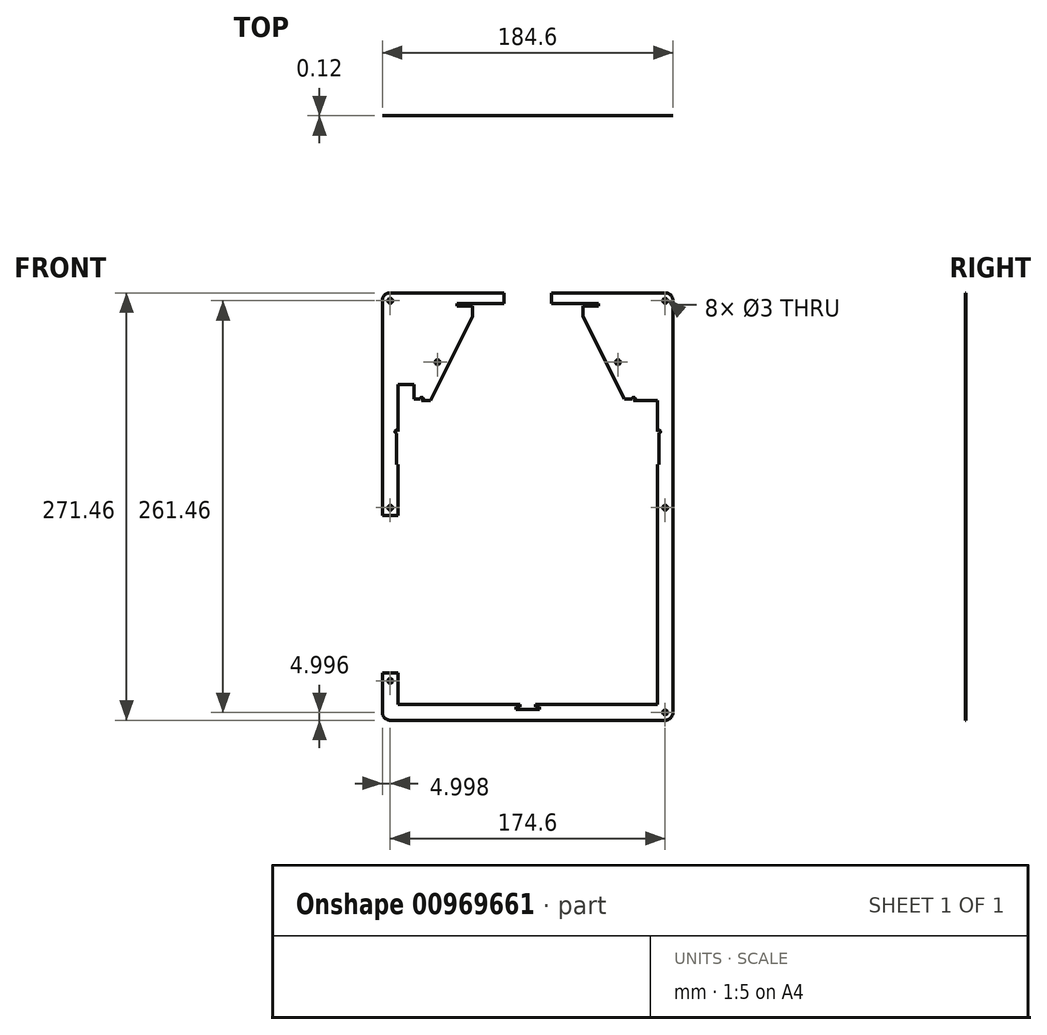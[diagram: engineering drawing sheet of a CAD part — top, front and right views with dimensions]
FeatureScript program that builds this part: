
annotation { "Feature Type Name" : "Feature", "Feature Type Description" : "" }
export const myFeature = defineFeature(function(context is Context, id is Id, definition is map)
    precondition{}
    {
        {
            var Q0;
            Q0=qCreatedBy(makeId("Front.planeOp"),FACE);
            var sketch = newSketch(context, id + "F0", { "sketchPlane" : qUnion([Q0])});
            skLineSegment(sketch, "E0.bottom", {"start": v(-64.57, 145.19) * mm, "end": v(110.03, 145.19) * mm});
            skLineSegment(sketch, "E0.top", {"start": v(-64.57, -126.27) * mm, "end": v(110.03, -126.27) * mm});
            skLineSegment(sketch, "E0.left", {"start": v(-69.57, 140.19) * mm, "end": v(-69.57, -121.27) * mm});
            skLineSegment(sketch, "E0.right", {"start": v(115.03, 140.19) * mm, "end": v(115.03, -121.27) * mm});
            skPoint(sketch, "E1.visualSharp", {"position": v(-69.57, 145.19) * mm});
            skArc(sketch, "E1.filletArc", {"start": v(-64.57, 145.19) * mm, "mid": v(-68.1, 143.72) * mm, "end": v(-69.57, 140.19) * mm});
            skPoint(sketch, "E2.visualSharp", {"position": v(115.03, 145.19) * mm});
            skArc(sketch, "E2.filletArc", {"start": v(115.03, 140.19) * mm, "mid": v(113.56, 143.72) * mm, "end": v(110.03, 145.19) * mm});
            skPoint(sketch, "E3.visualSharp", {"position": v(-69.57, -126.27) * mm});
            skArc(sketch, "E3.filletArc", {"start": v(-69.57, -121.27) * mm, "mid": v(-68.1, -124.8) * mm, "end": v(-64.57, -126.27) * mm});
            skPoint(sketch, "E4.visualSharp", {"position": v(115.03, -126.27) * mm});
            skArc(sketch, "E4.filletArc", {"start": v(110.03, -126.27) * mm, "mid": v(113.56, -124.8) * mm, "end": v(115.03, -121.27) * mm});
            skCircle(sketch, "E5", {"center": v(-64.57, 140.19) * mm, "radius": 1.5 * mm});
            skCircle(sketch, "E6", {"center": v(110.03, 140.19) * mm, "radius": 1.5 * mm});
            skCircle(sketch, "E7", {"center": v(110.03, -121.27) * mm, "radius": 1.5 * mm});
            skCircle(sketch, "E8", {"center": v(-64.57, -101.27) * mm, "radius": 1.5 * mm});
            skLineSegment(sketch, "E9.bottom", {"start": v(-59.57, 135.19) * mm, "end": v(105.03, 135.19) * mm});
            skLineSegment(sketch, "E9.top", {"start": v(-59.57, -116.27) * mm, "end": v(105.03, -116.27) * mm});
            skLineSegment(sketch, "E9.left", {"start": v(-59.57, 135.19) * mm, "end": v(-59.57, -116.27) * mm});
            skLineSegment(sketch, "E9.right", {"start": v(105.03, 135.19) * mm, "end": v(105.03, -116.27) * mm});
            skLineSegment(sketch, "E10.bottom", {"start": v(17.73, -116.27) * mm, "end": v(27.73, -116.27) * mm});
            skLineSegment(sketch, "E10.top", {"start": v(17.73, -117.75) * mm, "end": v(27.73, -117.75) * mm});
            skLineSegment(sketch, "E10.left", {"start": v(17.73, -116.27) * mm, "end": v(17.73, -117.75) * mm});
            skLineSegment(sketch, "E10.right", {"start": v(27.73, -116.27) * mm, "end": v(27.73, -117.75) * mm});
            skLineSegment(sketch, "E11.bottom", {"start": v(15.23, -117.75) * mm, "end": v(30.23, -117.75) * mm});
            skLineSegment(sketch, "E11.top", {"start": v(15.23, -119.35) * mm, "end": v(30.23, -119.35) * mm});
            skLineSegment(sketch, "E11.left", {"start": v(15.23, -117.75) * mm, "end": v(15.23, -119.35) * mm});
            skLineSegment(sketch, "E11.right", {"start": v(30.23, -117.75) * mm, "end": v(30.23, -119.35) * mm});
            skLineSegment(sketch, "E12.bottom", {"start": v(-12.27, 135.19) * mm, "end": v(57.73, 135.19) * mm});
            skLineSegment(sketch, "E12.top", {"start": v(-12.27, 136.79) * mm, "end": v(57.73, 136.79) * mm});
            skLineSegment(sketch, "E12.left", {"start": v(-12.27, 135.19) * mm, "end": v(-12.27, 136.79) * mm});
            skLineSegment(sketch, "E12.right", {"start": v(57.73, 135.19) * mm, "end": v(57.73, 136.79) * mm});
            skLineSegment(sketch, "E13.bottom", {"start": v(-22.27, 138.49) * mm, "end": v(67.73, 138.49) * mm});
            skLineSegment(sketch, "E13.top", {"start": v(-22.27, 136.79) * mm, "end": v(67.73, 136.79) * mm});
            skLineSegment(sketch, "E13.left", {"start": v(-22.27, 138.49) * mm, "end": v(-22.27, 136.79) * mm});
            skLineSegment(sketch, "E13.right", {"start": v(67.73, 138.49) * mm, "end": v(67.73, 136.79) * mm});
            skLineSegment(sketch, "E14.bottom", {"start": v(7.73, 145.19) * mm, "end": v(37.73, 145.19) * mm});
            skLineSegment(sketch, "E14.top", {"start": v(7.73, 138.49) * mm, "end": v(37.73, 138.49) * mm});
            skLineSegment(sketch, "E14.left", {"start": v(7.73, 145.19) * mm, "end": v(7.73, 138.49) * mm});
            skLineSegment(sketch, "E14.right", {"start": v(37.73, 145.19) * mm, "end": v(37.73, 138.49) * mm});
            skLineSegment(sketch, "E15.bottom", {"start": v(-59.57, 36.13) * mm, "end": v(105.03, 36.13) * mm});
            skLineSegment(sketch, "E15.top", {"start": v(-59.57, 35.13) * mm, "end": v(105.03, 35.13) * mm});
            skLineSegment(sketch, "E15.left", {"start": v(-59.57, 36.13) * mm, "end": v(-59.57, 35.13) * mm});
            skLineSegment(sketch, "E15.right", {"start": v(105.03, 36.13) * mm, "end": v(105.03, 35.13) * mm});
            skLineSegment(sketch, "E16.bottom", {"start": v(-62.57, 35.13) * mm, "end": v(108.03, 35.13) * mm});
            skLineSegment(sketch, "E16.top", {"start": v(-62.57, 33.13) * mm, "end": v(108.03, 33.13) * mm});
            skLineSegment(sketch, "E16.left", {"start": v(-62.57, 35.13) * mm, "end": v(-62.57, 33.13) * mm});
            skLineSegment(sketch, "E16.right", {"start": v(108.03, 35.13) * mm, "end": v(108.03, 33.13) * mm});
            skLineSegment(sketch, "E17.bottom", {"start": v(108.03, 33.13) * mm, "end": v(105.03, 33.13) * mm});
            skLineSegment(sketch, "E17.top", {"start": v(108.03, 34.53) * mm, "end": v(105.03, 34.53) * mm});
            skLineSegment(sketch, "E17.left", {"start": v(108.03, 33.13) * mm, "end": v(108.03, 34.53) * mm});
            skLineSegment(sketch, "E17.right", {"start": v(105.03, 33.13) * mm, "end": v(105.03, 34.53) * mm});
            skLineSegment(sketch, "E18.bottom", {"start": v(-62.57, 33.13) * mm, "end": v(-59.57, 33.13) * mm});
            skLineSegment(sketch, "E18.top", {"start": v(-62.57, 34.53) * mm, "end": v(-59.57, 34.53) * mm});
            skLineSegment(sketch, "E18.left", {"start": v(-62.57, 33.13) * mm, "end": v(-62.57, 34.53) * mm});
            skLineSegment(sketch, "E18.right", {"start": v(-59.57, 33.13) * mm, "end": v(-59.57, 34.53) * mm});
            skLineSegment(sketch, "E19.top", {"start": v(-59.57, 66.13) * mm, "end": v(105.03, 66.13) * mm});
            skLineSegment(sketch, "E19.left", {"start": v(-59.57, 36.13) * mm, "end": v(-59.57, 66.13) * mm});
            skLineSegment(sketch, "E19.right", {"start": v(105.03, 36.13) * mm, "end": v(105.03, 66.13) * mm});
            skLineSegment(sketch, "E20.top", {"start": v(-59.57, 76.88) * mm, "end": v(105.03, 76.88) * mm});
            skLineSegment(sketch, "E20.left", {"start": v(-59.57, 36.13) * mm, "end": v(-59.57, 76.88) * mm});
            skLineSegment(sketch, "E20.right", {"start": v(105.03, 36.13) * mm, "end": v(105.03, 76.88) * mm});
            skLineSegment(sketch, "E21.bottom", {"start": v(-52.27, 66.13) * mm, "end": v(97.73, 66.13) * mm});
            skLineSegment(sketch, "E21.top", {"start": v(-52.27, 36.13) * mm, "end": v(97.73, 36.13) * mm});
            skLineSegment(sketch, "E21.left", {"start": v(-52.27, 66.13) * mm, "end": v(-52.27, 36.13) * mm});
            skLineSegment(sketch, "E21.right", {"start": v(97.73, 66.13) * mm, "end": v(97.73, 36.13) * mm});
            skLineSegment(sketch, "E22.bottom", {"start": v(-55.27, 36.13) * mm, "end": v(100.73, 36.13) * mm});
            skLineSegment(sketch, "E22.top", {"start": v(-55.27, 69.13) * mm, "end": v(100.73, 69.13) * mm});
            skLineSegment(sketch, "E22.left", {"start": v(-55.27, 36.13) * mm, "end": v(-55.27, 69.13) * mm});
            skLineSegment(sketch, "E22.right", {"start": v(100.73, 36.13) * mm, "end": v(100.73, 69.13) * mm});
            skLineSegment(sketch, "E23.bottom", {"start": v(-58.27, 72.13) * mm, "end": v(103.73, 72.13) * mm});
            skLineSegment(sketch, "E23.top", {"start": v(-58.27, 33.13) * mm, "end": v(103.73, 33.13) * mm});
            skLineSegment(sketch, "E23.left", {"start": v(-58.27, 72.13) * mm, "end": v(-58.27, 33.13) * mm});
            skLineSegment(sketch, "E23.right", {"start": v(103.73, 72.13) * mm, "end": v(103.73, 33.13) * mm});
            skLineSegment(sketch, "E24.top", {"start": v(-12.27, 130.19) * mm, "end": v(57.73, 130.19) * mm});
            skLineSegment(sketch, "E24.left", {"start": v(-12.27, 135.19) * mm, "end": v(-12.27, 130.19) * mm});
            skLineSegment(sketch, "E24.right", {"start": v(57.73, 135.19) * mm, "end": v(57.73, 130.19) * mm});
            skLineSegment(sketch, "E25.bottom", {"start": v(-59.57, 33.13) * mm, "end": v(105.03, 33.13) * mm});
            skLineSegment(sketch, "E25.top", {"start": v(-59.57, 23.13) * mm, "end": v(105.03, 23.13) * mm});
            skLineSegment(sketch, "E25.left", {"start": v(-59.57, 33.13) * mm, "end": v(-59.57, 23.13) * mm});
            skLineSegment(sketch, "E25.right", {"start": v(105.03, 33.13) * mm, "end": v(105.03, 23.13) * mm});
            skLineSegment(sketch, "E26.bottom", {"start": v(-69.57, -96.27) * mm, "end": v(-59.57, -96.27) * mm});
            skLineSegment(sketch, "E26.top", {"start": v(-69.57, 3.73) * mm, "end": v(-59.57, 3.73) * mm});
            skLineSegment(sketch, "E26.left", {"start": v(-69.57, -96.27) * mm, "end": v(-69.57, 3.73) * mm});
            skLineSegment(sketch, "E26.right", {"start": v(-59.57, -96.27) * mm, "end": v(-59.57, 3.73) * mm});
            skLineSegment(sketch, "E27", {"start": v(-12.27, 130.19) * mm, "end": v(-59.57, 36.13) * mm});
            skLineSegment(sketch, "E28", {"start": v(57.73, 130.19) * mm, "end": v(105.03, 36.13) * mm});
            skCircle(sketch, "E29", {"center": v(-34.57, 101.13) * mm, "radius": 1.5 * mm});
            skCircle(sketch, "E30", {"center": v(80.03, 101.13) * mm, "radius": 1.5 * mm});
            skLineSegment(sketch, "E31.top", {"start": v(7.73, 23.13) * mm, "end": v(37.73, 23.13) * mm});
            skLineSegment(sketch, "E31.left", {"start": v(7.73, 138.49) * mm, "end": v(7.73, 23.13) * mm});
            skLineSegment(sketch, "E31.right", {"start": v(37.73, 138.49) * mm, "end": v(37.73, 23.13) * mm});
            skLineSegment(sketch, "E32.bottom", {"start": v(-59.57, 76.88) * mm, "end": v(7.73, 76.88) * mm});
            skLineSegment(sketch, "E33.bottom", {"start": v(-59.57, 36.13) * mm, "end": v(-39.57, 36.13) * mm});
            skLineSegment(sketch, "E33.top", {"start": v(-59.57, 76.88) * mm, "end": v(-39.57, 76.88) * mm});
            skLineSegment(sketch, "E33.right", {"start": v(-39.57, 36.13) * mm, "end": v(-39.57, 76.88) * mm});
            skLineSegment(sketch, "E34.bottom", {"start": v(105.03, 76.88) * mm, "end": v(85.03, 76.88) * mm});
            skLineSegment(sketch, "E34.top", {"start": v(105.03, 36.13) * mm, "end": v(85.03, 36.13) * mm});
            skLineSegment(sketch, "E34.left", {"start": v(105.03, 76.88) * mm, "end": v(105.03, 36.13) * mm});
            skLineSegment(sketch, "E34.right", {"start": v(85.03, 76.88) * mm, "end": v(85.03, 36.13) * mm});
            skLineSegment(sketch, "E35.bottom", {"start": v(105.03, 23.13) * mm, "end": v(95.03, 23.13) * mm});
            skLineSegment(sketch, "E35.top", {"start": v(105.03, 36.13) * mm, "end": v(95.03, 36.13) * mm});
            skLineSegment(sketch, "E35.left", {"start": v(105.03, 23.13) * mm, "end": v(105.03, 36.13) * mm});
            skLineSegment(sketch, "E35.right", {"start": v(95.03, 23.13) * mm, "end": v(95.03, 36.13) * mm});
            skLineSegment(sketch, "E36.bottom", {"start": v(-49.57, 23.13) * mm, "end": v(-59.57, 23.13) * mm});
            skLineSegment(sketch, "E36.top", {"start": v(-49.57, 36.13) * mm, "end": v(-59.57, 36.13) * mm});
            skLineSegment(sketch, "E36.left", {"start": v(-49.57, 23.13) * mm, "end": v(-49.57, 36.13) * mm});
            skLineSegment(sketch, "E36.right", {"start": v(-59.57, 23.13) * mm, "end": v(-59.57, 36.13) * mm});
            skLineSegment(sketch, "E37.top", {"start": v(-49.57, 86.93) * mm, "end": v(-59.57, 86.93) * mm});
            skLineSegment(sketch, "E37.left", {"start": v(-49.57, 36.13) * mm, "end": v(-49.57, 86.93) * mm});
            skLineSegment(sketch, "E37.right", {"start": v(-59.57, 36.13) * mm, "end": v(-59.57, 86.93) * mm});
            skCircle(sketch, "E38", {"center": v(-64.57, 8.73) * mm, "radius": 1.5 * mm});
            skCircle(sketch, "E39", {"center": v(110.03, 8.73) * mm, "radius": 1.5 * mm});
            skLineSegment(sketch, "E40.bottom", {"start": v(-60.57, 36.13) * mm, "end": v(106.03, 36.13) * mm});
            skLineSegment(sketch, "E40.top", {"start": v(-60.57, 77.88) * mm, "end": v(106.03, 77.88) * mm});
            skLineSegment(sketch, "E40.left", {"start": v(-60.57, 36.13) * mm, "end": v(-60.57, 77.88) * mm});
            skLineSegment(sketch, "E40.right", {"start": v(106.03, 36.13) * mm, "end": v(106.03, 77.88) * mm});
            skCircle(sketch, "E41", {"center": v(-60.57, 57) * mm, "radius": 1 * mm});
            skCircle(sketch, "E42", {"center": v(106.03, 57.05) * mm, "radius": 1 * mm});
            skCircle(sketch, "E43", {"center": v(-5.04, 77.88) * mm, "radius": 1 * mm});
            skCircle(sketch, "E44", {"center": v(50.5, 77.88) * mm, "radius": 1 * mm});
            skLineSegment(sketch, "E45.bottom", {"start": v(-54.57, 18.13) * mm, "end": v(100.03, 18.13) * mm});
            skLineSegment(sketch, "E45.top", {"start": v(-54.57, -111.27) * mm, "end": v(100.03, -111.27) * mm});
            skLineSegment(sketch, "E45.left", {"start": v(-54.57, 18.13) * mm, "end": v(-54.57, -111.27) * mm});
            skLineSegment(sketch, "E45.right", {"start": v(100.03, 18.13) * mm, "end": v(100.03, -111.27) * mm});
            skCircle(sketch, "E46", {"center": v(-54.57, 18.13) * mm, "radius": 1 * mm});
            skCircle(sketch, "E47", {"center": v(100.03, 18.13) * mm, "radius": 1 * mm});
            skCircle(sketch, "E48", {"center": v(100.03, -111.27) * mm, "radius": 1 * mm});
            skCircle(sketch, "E49", {"center": v(-54.57, -111.27) * mm, "radius": 1 * mm});
            skCircle(sketch, "E50", {"center": v(-44.57, 77.88) * mm, "radius": 1 * mm});
            skCircle(sketch, "E51", {"center": v(90.03, 77.88) * mm, "radius": 1 * mm});
            skSolve(sketch);
        }
        {
            var Q0;
            Q0=makeQuery(id+"F0.imprint","IMPRINT",FACE,{"disambiguationData":[TD([[makeQuery(id+"F0.imprint","IMPRINT",EDGE,{"derivedFrom":sQuery(id+"F0.wireOp",EDGE,"E0.top")}),1.0]])]});
            var Q1;
            {var subQ0=sQuery(id+"F0.wireOp",EDGE,"E16.left");Q1=makeQuery(id+"F0.imprint","IMPRINT",FACE,{"disambiguationData":[TD([[makeQuery(id+"F0.imprint","IMPRINT",EDGE,{"derivedFrom":subQ0}),1.0]])]});}
            var Q2;
            {var subQ0=sQuery(id+"F0.wireOp",EDGE,"E16.right");Q2=makeQuery(id+"F0.imprint","IMPRINT",FACE,{"disambiguationData":[TD([[makeQuery(id+"F0.imprint","IMPRINT",EDGE,{"derivedFrom":subQ0}),-1.0]])]});}
            var Q3;
            {var subQ7=sQuery(id+"F0.wireOp",EDGE,"E24.right");Q3=makeQuery(id+"F0.imprint","IMPRINT",FACE,{"disambiguationData":[TD([[makeQuery(id+"F0.imprint","IMPRINT",EDGE,{"derivedFrom":subQ7}),1.0]])]});}
            var Q4;
            {var subQ0=sQuery(id+"F0.wireOp",EDGE,"E42");var subQ1=sQuery(id+"F0.wireOp",EDGE,"E40.right");var subQ2=makeQuery(id+"F0.imprint","INTERSECT",VERTEX,{"disambiguationData":[OD(0.0)],"derivedFrom":[subQ1,subQ0]});Q4=makeQuery(id+"F0.imprint","IMPRINT",FACE,{"disambiguationData":[TD([[makeQuery(id+"F0.imprint","IMPRINT",EDGE,{"disambiguationData":[TD([[subQ2,-1.0]])],"derivedFrom":subQ1}),-1.0]])]});}
            var Q5;
            {var subQ0=sQuery(id+"F0.wireOp",EDGE,"E41");var subQ1=sQuery(id+"F0.wireOp",EDGE,"E40.left");var subQ2=makeQuery(id+"F0.imprint","INTERSECT",VERTEX,{"disambiguationData":[OD(0.0)],"derivedFrom":[subQ1,subQ0]});Q5=makeQuery(id+"F0.imprint","IMPRINT",FACE,{"disambiguationData":[TD([[makeQuery(id+"F0.imprint","IMPRINT",EDGE,{"disambiguationData":[TD([[subQ2,-1.0]])],"derivedFrom":subQ1}),1.0]])]});}
            var Q6;
            {var subQ0=sQuery(id+"F0.wireOp",EDGE,"E42");var subQ1=sQuery(id+"F0.wireOp",EDGE,"E40.right");var subQ2=makeQuery(id+"F0.imprint","INTERSECT",VERTEX,{"disambiguationData":[OD(0.0)],"derivedFrom":[subQ1,subQ0]});Q6=makeQuery(id+"F0.imprint","IMPRINT",FACE,{"disambiguationData":[TD([[makeQuery(id+"F0.imprint","IMPRINT",EDGE,{"disambiguationData":[TD([[subQ2,-1.0]])],"derivedFrom":subQ1}),1.0]])]});}
            var Q7;
            {var subQ0=sQuery(id+"F0.wireOp",EDGE,"E41");var subQ1=sQuery(id+"F0.wireOp",EDGE,"E40.left");var subQ2=makeQuery(id+"F0.imprint","INTERSECT",VERTEX,{"disambiguationData":[OD(0.0)],"derivedFrom":[subQ1,subQ0]});Q7=makeQuery(id+"F0.imprint","IMPRINT",FACE,{"disambiguationData":[TD([[makeQuery(id+"F0.imprint","IMPRINT",EDGE,{"disambiguationData":[TD([[subQ2,-1.0]])],"derivedFrom":subQ1}),-1.0]])]});}
            var Q8;
            {var subQ6=sQuery(id+"F0.wireOp",EDGE,"E1.filletArc");Q8=makeQuery(id+"F0.imprint","IMPRINT",FACE,{"disambiguationData":[TD([[makeQuery(id+"F0.imprint","IMPRINT",EDGE,{"derivedFrom":subQ6}),1.0]])]});}
            var Q9;
            {var subQ5=sQuery(id+"F0.wireOp",EDGE,"E24.left");Q9=makeQuery(id+"F0.imprint","IMPRINT",FACE,{"disambiguationData":[TD([[makeQuery(id+"F0.imprint","IMPRINT",EDGE,{"derivedFrom":subQ5}),-1.0]])]});}
            var Q10;
            {var subQ0=sQuery(id+"F0.wireOp",EDGE,"E50");var subQ1=sQuery(id+"F0.wireOp",EDGE,"E40.top");var subQ2=makeQuery(id+"F0.imprint","INTERSECT",VERTEX,{"disambiguationData":[OD(0.0)],"derivedFrom":[subQ1,subQ0]});Q10=makeQuery(id+"F0.imprint","IMPRINT",FACE,{"disambiguationData":[TD([[makeQuery(id+"F0.imprint","IMPRINT",EDGE,{"disambiguationData":[TD([[subQ2,-1.0]])],"derivedFrom":subQ1}),-1.0]])]});}
            var Q11;
            {var subQ0=sQuery(id+"F0.wireOp",EDGE,"E50");var subQ1=sQuery(id+"F0.wireOp",EDGE,"E40.top");var subQ2=makeQuery(id+"F0.imprint","INTERSECT",VERTEX,{"disambiguationData":[OD(0.0)],"derivedFrom":[subQ1,subQ0]});Q11=makeQuery(id+"F0.imprint","IMPRINT",FACE,{"disambiguationData":[TD([[makeQuery(id+"F0.imprint","IMPRINT",EDGE,{"disambiguationData":[TD([[subQ2,-1.0]])],"derivedFrom":subQ1}),1.0]])]});}
            var Q12;
            {var subQ0=sQuery(id+"F0.wireOp",EDGE,"E51");var subQ1=sQuery(id+"F0.wireOp",EDGE,"E40.top");var subQ2=makeQuery(id+"F0.imprint","INTERSECT",VERTEX,{"disambiguationData":[OD(0.0)],"derivedFrom":[subQ1,subQ0]});Q12=makeQuery(id+"F0.imprint","IMPRINT",FACE,{"disambiguationData":[TD([[makeQuery(id+"F0.imprint","IMPRINT",EDGE,{"disambiguationData":[TD([[subQ2,-1.0]])],"derivedFrom":subQ1}),-1.0]])]});}
            var Q13;
            {var subQ0=sQuery(id+"F0.wireOp",EDGE,"E51");var subQ1=sQuery(id+"F0.wireOp",EDGE,"E40.top");var subQ2=makeQuery(id+"F0.imprint","INTERSECT",VERTEX,{"disambiguationData":[OD(0.0)],"derivedFrom":[subQ1,subQ0]});Q13=makeQuery(id+"F0.imprint","IMPRINT",FACE,{"disambiguationData":[TD([[makeQuery(id+"F0.imprint","IMPRINT",EDGE,{"disambiguationData":[TD([[subQ2,-1.0]])],"derivedFrom":subQ1}),1.0]])]});}
            extrude(context, id + "F1", {"entities" : qUnion([Q0, Q1, Q2, Q3, Q4, Q5, Q6, Q7, Q8, Q9, Q10, Q11, Q12, Q13]), "depth" : .118 * mm, "offsetDistance" : 25 * mm});
        }
    });
